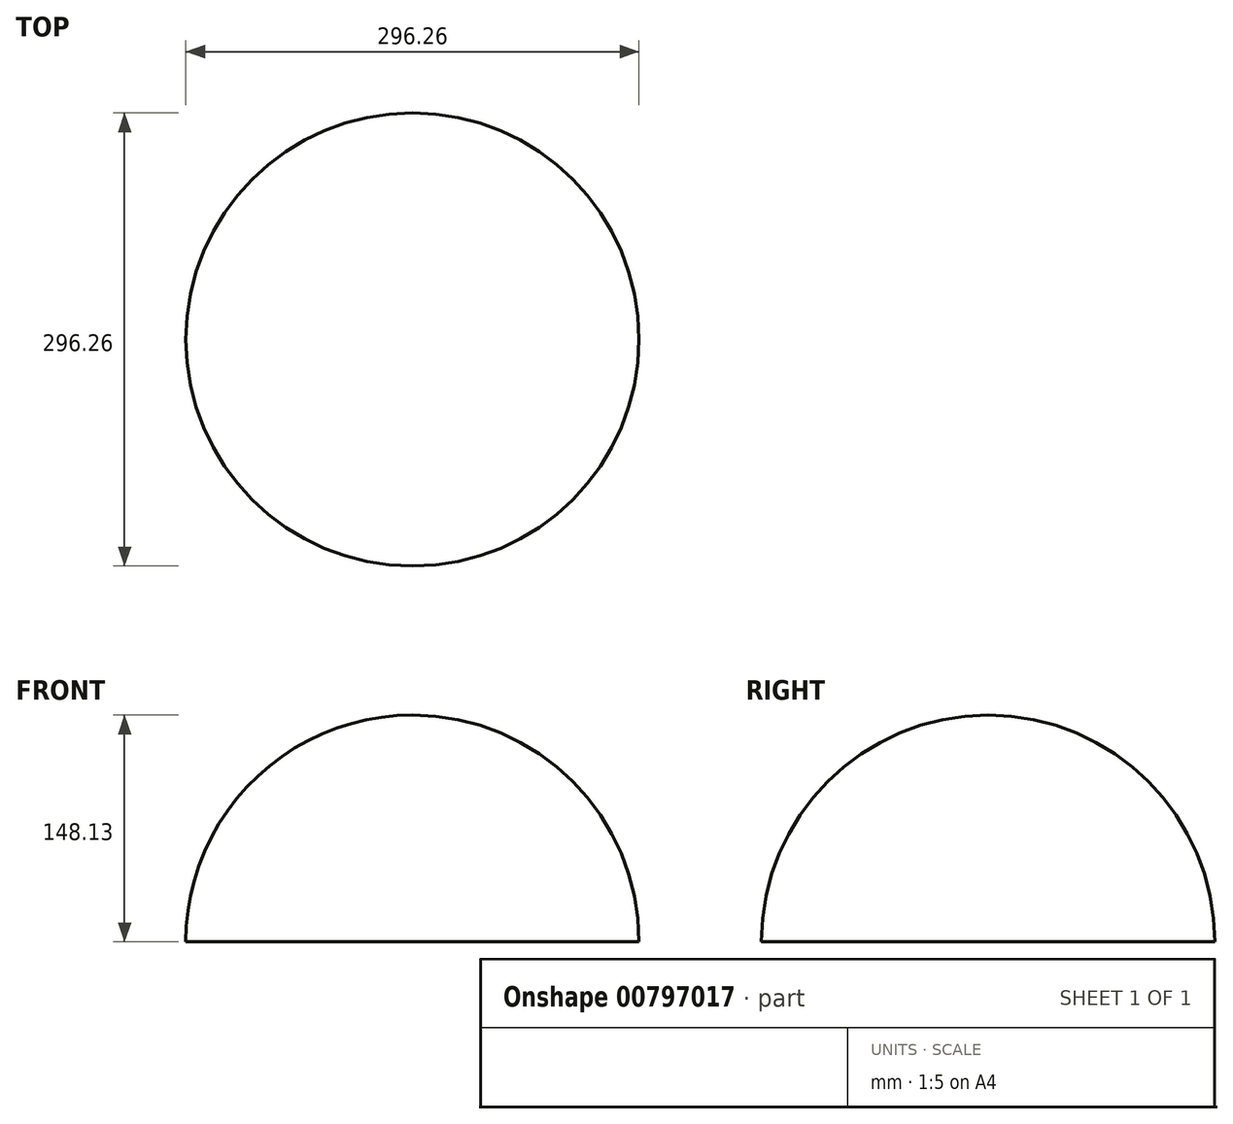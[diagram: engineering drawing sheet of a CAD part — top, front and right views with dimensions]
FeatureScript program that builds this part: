
annotation { "Feature Type Name" : "Feature", "Feature Type Description" : "" }
export const myFeature = defineFeature(function(context is Context, id is Id, definition is map)
    precondition{}
    {
        {
            var Q0;
            Q0=qCreatedBy(makeId("Front.planeOp"),FACE);
            var sketch = newSketch(context, id + "F0", { "sketchPlane" : qUnion([Q0])});
            skLineSegment(sketch, "E0", {"start": v(0, 0) * mm, "end": v(0, 148.13) * mm});
            skLineSegment(sketch, "E1", {"start": v(0, 0) * mm, "end": v(-148.13, 0) * mm});
            skArc(sketch, "E2", {"start": v(-148.13, 0) * mm, "mid": v(-104.74, 104.74) * mm, "end": v(0, 148.13) * mm});
            skSolve(sketch);
        }
        {
            var Q0;
            Q0 = qSketchRegion(id + "F0", true);
            var Q1;
            Q1=sQuery(id+"F0.wireOp",EDGE,"E0");
            revolve(context, id + "F1", {"surfaceOperationType" : NewSurfaceOperationType.NEW, "entities" : qUnion([Q0]), "axis" : qUnion([Q1]), "revolveType" : RevolveType.FULL});
        }
    });
